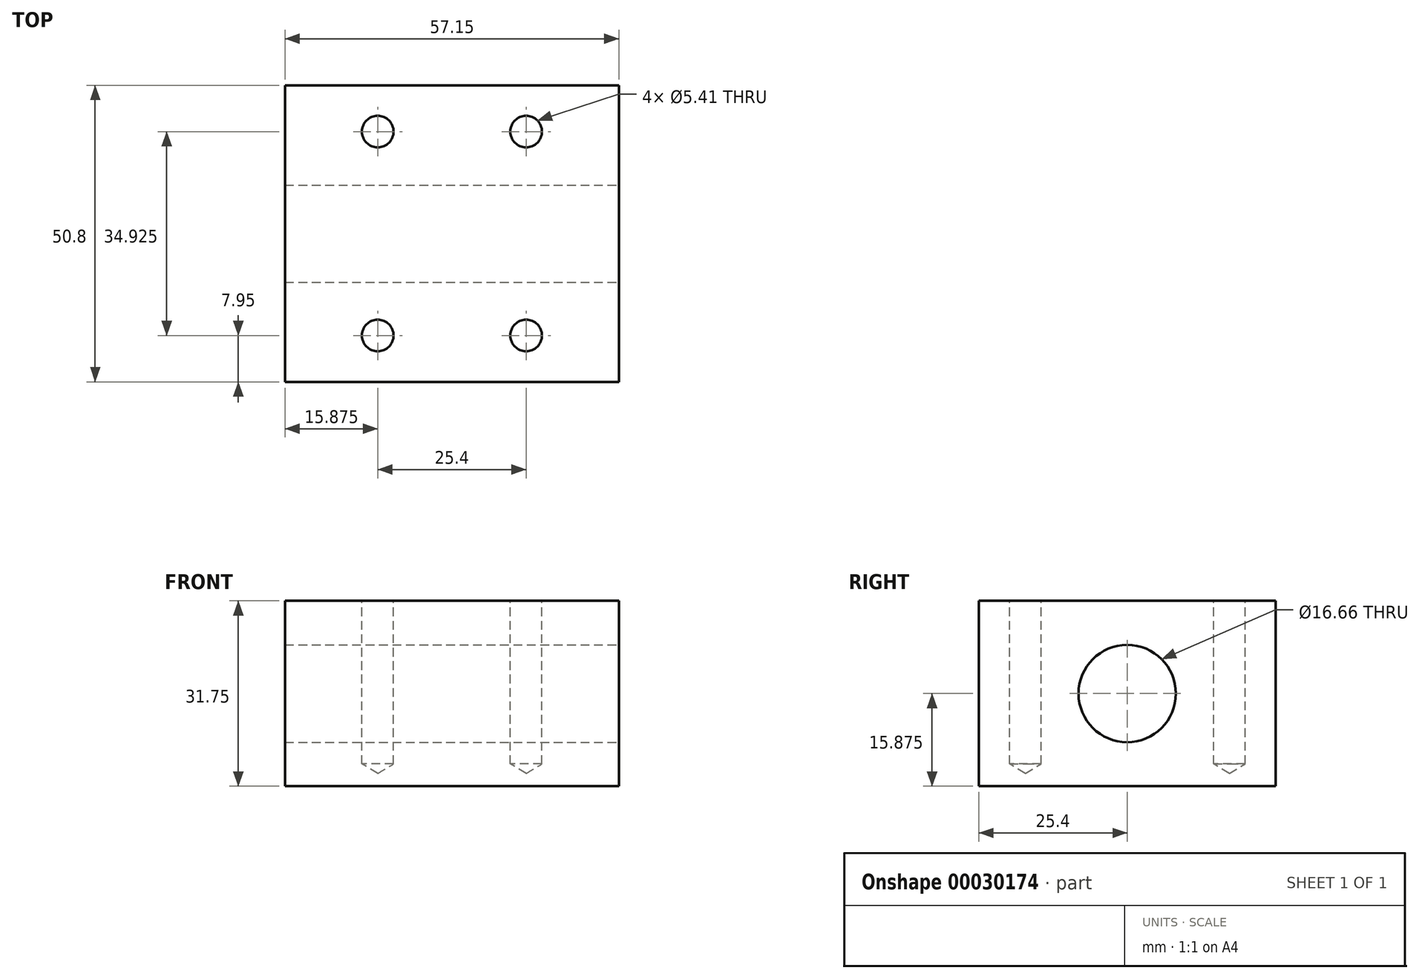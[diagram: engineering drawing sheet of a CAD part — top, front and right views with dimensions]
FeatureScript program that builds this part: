
annotation { "Feature Type Name" : "Feature", "Feature Type Description" : "" }
export const myFeature = defineFeature(function(context is Context, id is Id, definition is map)
    precondition{}
    {
        {
            var Q0;
            Q0=qCreatedBy(makeId("Top.planeOp"),FACE);
            var sketch = newSketch(context, id + "F0", { "sketchPlane" : qUnion([Q0])});
            skLineSegment(sketch, "E0.bottom", {"start": v(0, 0) * mm, "end": v(-57.15, 0) * mm});
            skLineSegment(sketch, "E0.top", {"start": v(0, -50.8) * mm, "end": v(-57.15, -50.8) * mm});
            skLineSegment(sketch, "E0.left", {"start": v(0, 0) * mm, "end": v(0, -50.8) * mm});
            skLineSegment(sketch, "E0.right", {"start": v(-57.15, 0) * mm, "end": v(-57.15, -50.8) * mm});
            skPoint(sketch, "E1", {"position": v(-15.88, -7.92) * mm});
            skPoint(sketch, "E2", {"position": v(-41.27, -7.92) * mm});
            skPoint(sketch, "E3", {"position": v(-15.87, -42.85) * mm});
            skPoint(sketch, "E4", {"position": v(-41.27, -42.85) * mm});
            skSolve(sketch);
        }
        {
            var Q0;
            Q0=makeQuery(id+"F0.imprint","IMPRINT",FACE,{"disambiguationData":[TD([[makeQuery(id+"F0.imprint","IMPRINT",EDGE,{"derivedFrom":sQuery(id+"F0.wireOp",EDGE,"E0.bottom")}),1.0]])]});
            extrude(context, id + "F1", {"entities" : qUnion([Q0]), "oppositeDirection" : true, "depth" : 31.75 * mm});
        }
        {
            var Q0;
            Q0=sQuery(id+"F0.wireOp",VERTEX,"E1");
            var Q1;
            Q1=sQuery(id+"F0.wireOp",VERTEX,"E3");
            var Q2;
            Q2=sQuery(id+"F0.wireOp",VERTEX,"E4");
            var Q3;
            Q3=sQuery(id+"F0.wireOp",VERTEX,"E2");
            var Q4;
            Q4=makeQuery(id+"F1.opExtrude","SWEPT_BODY",BODY,{"disambiguationData":[OSD([sQuery(id+"F0.wireOp",EDGE,"E0.bottom"),sQuery(id+"F0.wireOp",EDGE,"E0.top"),sQuery(id+"F0.wireOp",EDGE,"E0.left"),sQuery(id+"F0.wireOp",EDGE,"E0.right")])]});
            hole(context, id + "F2", {"style" : HoleStyle.SIMPLE, "holeDiameter" : 5.4 * mm, "endStyle" : HoleEndStyle.BLIND, "holeDepth" : 27.94 * mm, "locations" : qUnion([Q0, Q1, Q2, Q3]), "scope" : qUnion([Q4])});
        }
        {
            var Q0;
            Q0=makeQuery(id+"F1.opExtrude","SWEPT_FACE",FACE,{"disambiguationData":[OSD([sQuery(id+"F0.wireOp",EDGE,"E0.left")])]});
            var sketch = newSketch(context, id + "F3", { "sketchPlane" : qUnion([Q0])});
            skCircle(sketch, "E5", {"center": v(-25.4, -15.88) * mm, "radius": 8.33 * mm});
            skSolve(sketch);
        }
        {
            var Q0;
            Q0=makeQuery(id+"F3.imprint","IMPRINT",FACE,{"disambiguationData":[TD([[makeQuery(id+"F3.imprint","IMPRINT",EDGE,{"derivedFrom":sQuery(id+"F3.wireOp",EDGE,"E5")}),1.0]])]});
            extrude(context, id + "F4", {"entities" : qUnion([Q0]), "operationType" : NewBodyOperationType.REMOVE, "endBound" : BoundingType.THROUGH_ALL, "oppositeDirection" : true, "depth" : 25.4 * mm});
        }
    });
